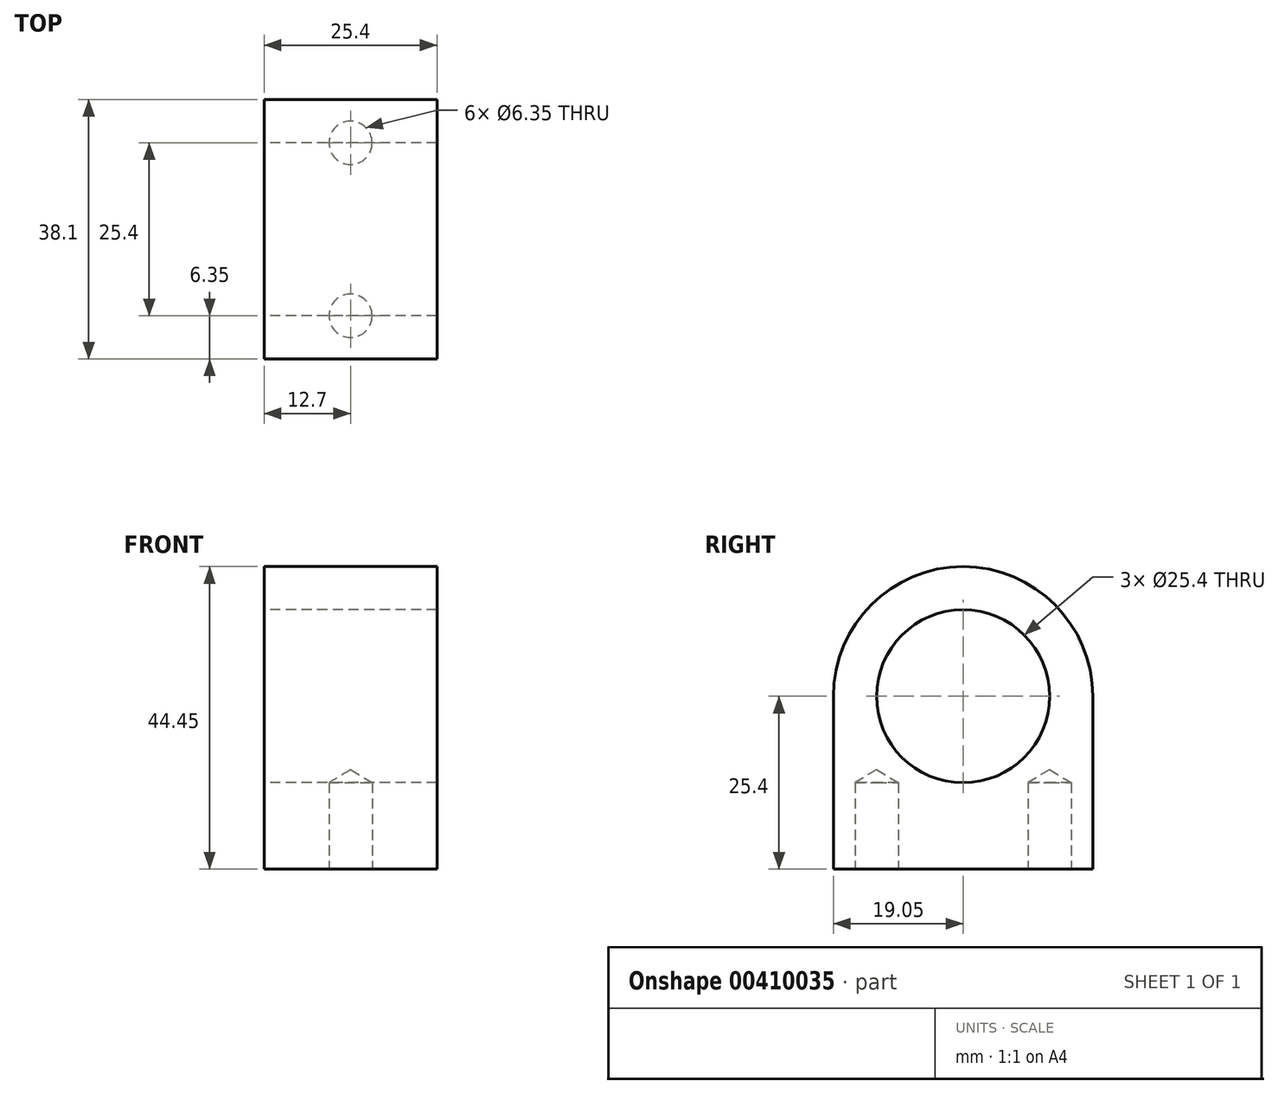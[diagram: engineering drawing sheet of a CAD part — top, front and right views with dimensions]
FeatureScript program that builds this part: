
annotation { "Feature Type Name" : "Feature", "Feature Type Description" : "" }
export const myFeature = defineFeature(function(context is Context, id is Id, definition is map)
    precondition{}
    {
        {
            var Q0;
            Q0=qCreatedBy(makeId("Right.planeOp"),FACE);
            var sketch = newSketch(context, id + "F0", { "sketchPlane" : qUnion([Q0])});
            skCircle(sketch, "E0", {"center": v(0, 0) * mm, "radius": 12.7 * mm});
            skArc(sketch, "E1", {"start": v(19.05, 0) * mm, "mid": v(0, 19.05) * mm, "end": v(-19.05, 0) * mm});
            skLineSegment(sketch, "E2", {"start": v(-19.05, 0) * mm, "end": v(-19.05, -25.4) * mm});
            skLineSegment(sketch, "E3", {"start": v(-19.05, -25.4) * mm, "end": v(19.05, -25.4) * mm});
            skLineSegment(sketch, "E4", {"start": v(19.05, -25.4) * mm, "end": v(19.05, 0) * mm});
            skSolve(sketch);
        }
        {
            var Q0;
            Q0=makeQuery(id+"F0.imprint","IMPRINT",FACE,{"disambiguationData":[TD([[makeQuery(id+"F0.imprint","IMPRINT",EDGE,{"derivedFrom":sQuery(id+"F0.wireOp",EDGE,"E0")}),-1.0]])]});
            extrude(context, id + "F1", {"entities" : qUnion([Q0]), "depth" : 25.4 * mm});
        }
        {
            var Q0;
            Q0=makeQuery(id+"F1.opExtrude","SWEPT_FACE",FACE,{"disambiguationData":[OSD([sQuery(id+"F0.wireOp",EDGE,"E3")])]});
            var sketch = newSketch(context, id + "F2", { "sketchPlane" : qUnion([Q0])});
            skPoint(sketch, "E5", {"position": v(12.7, 12.7) * mm});
            skPoint(sketch, "E5.positionSnap0", {"position": v(12.7, 19.05) * mm});
            skPoint(sketch, "E6", {"position": v(12.7, -12.7) * mm});
            skSolve(sketch);
        }
        {
            var Q0;
            Q0=sQuery(id+"F2.wireOp",VERTEX,"E5");
            var Q1;
            Q1=sQuery(id+"F2.wireOp",VERTEX,"E6");
            var Q2;
            Q2=makeQuery(id+"F1.opExtrude","SWEPT_BODY",BODY,{"disambiguationData":[OSD([sQuery(id+"F0.wireOp",EDGE,"E0"),sQuery(id+"F0.wireOp",EDGE,"E1"),sQuery(id+"F0.wireOp",EDGE,"E2"),sQuery(id+"F0.wireOp",EDGE,"E3"),sQuery(id+"F0.wireOp",EDGE,"E4")])]});
            hole(context, id + "F3", {"style" : HoleStyle.SIMPLE, "endStyle" : HoleEndStyle.BLIND, "holeDiameter" : 6.35 * mm, "holeDepth" : 12.7 * mm, "isTappedThrough" : true, "tappedDepth" : 12.7 * mm, "tapClearance" : 3, "locations" : qUnion([Q0, Q1]), "scope" : qUnion([Q2])});
        }
    });
